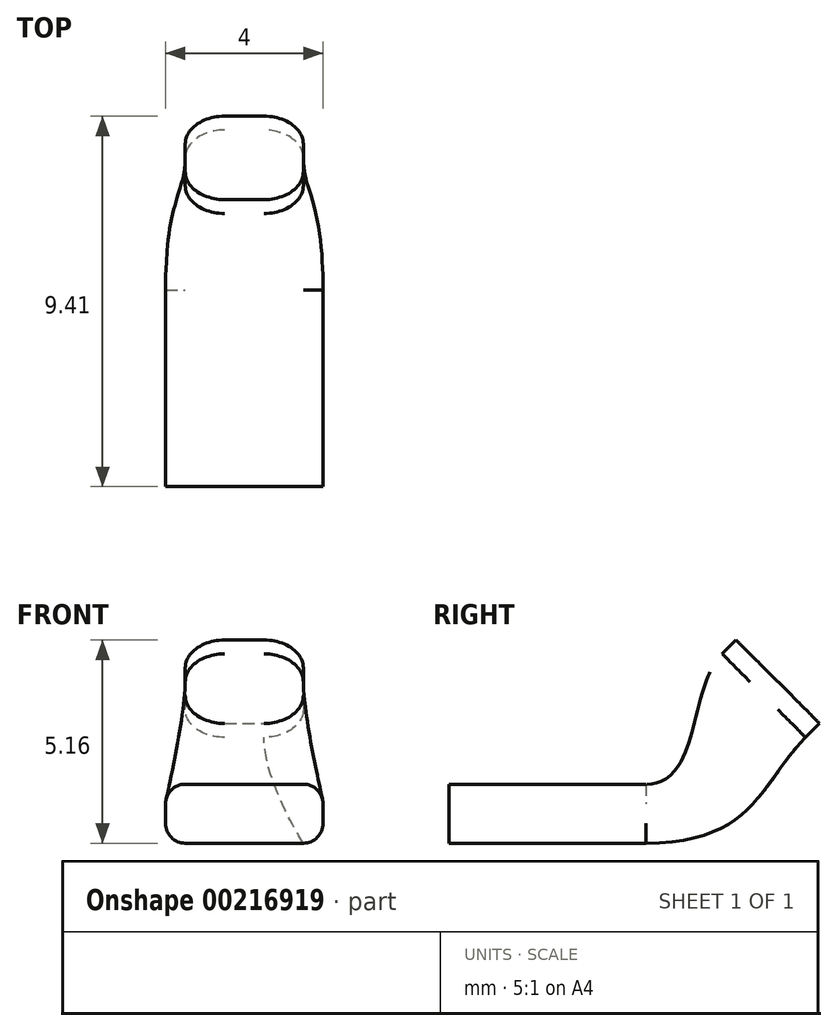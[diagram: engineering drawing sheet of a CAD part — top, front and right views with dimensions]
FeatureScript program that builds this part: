
annotation { "Feature Type Name" : "Feature", "Feature Type Description" : "" }
export const myFeature = defineFeature(function(context is Context, id is Id, definition is map)
    precondition{}
    {
        {
            var Q0;
            Q0=qCreatedBy(makeId("Right.planeOp"),FACE);
            var sketch = newSketch(context, id + "F0", { "sketchPlane" : qUnion([Q0])});
            skLineSegment(sketch, "E0", {"start": v(0, 0) * mm, "end": v(0, 5) * mm});
            skLineSegment(sketch, "E1", {"start": v(0, 5) * mm, "end": v(1, 5) * mm});
            skLineSegment(sketch, "E2", {"start": v(1, 5) * mm, "end": v(4.72, 1.28) * mm});
            skLineSegment(sketch, "E3", {"start": v(4.19, 0) * mm, "end": v(0, 0) * mm});
            skPoint(sketch, "E4.visualSharp", {"position": v(6, 0) * mm});
            skArc(sketch, "E4.filletArc", {"start": v(4.19, 0) * mm, "mid": v(4.88, 0.46) * mm, "end": v(4.72, 1.28) * mm});
            skSolve(sketch);
        }
        {
            var Q0;
            Q0=qCreatedBy(makeId("Front.planeOp"),FACE);
            var sketch = newSketch(context, id + "F1", { "sketchPlane" : qUnion([Q0])});
            skLineSegment(sketch, "E5.bottom", {"start": v(1.5, -0.75) * mm, "end": v(-1.5, -0.75) * mm});
            skLineSegment(sketch, "E5.top", {"start": v(1.5, 0.75) * mm, "end": v(-1.5, 0.75) * mm});
            skLineSegment(sketch, "E5.left", {"start": v(2, -0.25) * mm, "end": v(2, 0.25) * mm});
            skLineSegment(sketch, "E5.right", {"start": v(-2, -0.25) * mm, "end": v(-2, 0.25) * mm});
            skPoint(sketch, "E5.middle", {"position": v(0, 0) * mm});
            skPoint(sketch, "E6.visualSharp", {"position": v(2, 0.75) * mm});
            skArc(sketch, "E6.filletArc", {"start": v(2, 0.25) * mm, "mid": v(1.85, 0.6) * mm, "end": v(1.5, 0.75) * mm});
            skPoint(sketch, "E7.visualSharp", {"position": v(2, -0.75) * mm});
            skArc(sketch, "E7.filletArc", {"start": v(1.5, -0.75) * mm, "mid": v(1.85, -0.6) * mm, "end": v(2, -0.25) * mm});
            skPoint(sketch, "E8.visualSharp", {"position": v(-2, 0.75) * mm});
            skArc(sketch, "E8.filletArc", {"start": v(-1.5, 0.75) * mm, "mid": v(-1.85, 0.6) * mm, "end": v(-2, 0.25) * mm});
            skPoint(sketch, "E9.visualSharp", {"position": v(-2, -0.75) * mm});
            skArc(sketch, "E9.filletArc", {"start": v(-2, -0.25) * mm, "mid": v(-1.85, -0.6) * mm, "end": v(-1.5, -0.75) * mm});
            skSolve(sketch);
        }
        {
            var Q0;
            Q0=sQuery(id+"F0.wireOp",EDGE,"E2");
            cPlane(context, id + "F2", {"entities" : qUnion([Q0]), "cplaneType" : CPlaneType.LINE_ANGLE, "offset" : 25 * mm, "angle" : 0 * degree, "width" : 150 * mm, "height" : 150 * mm});
        }
        {
            var Q0;
            Q0=qCreatedBy(id+"F2.planeOp",FACE);
            var sketch = newSketch(context, id + "F3", { "sketchPlane" : qUnion([Q0])});
            skLineSegment(sketch, "E10.bottom", {"start": v(0.5, 1.5) * mm, "end": v(-0.5, 1.5) * mm});
            skLineSegment(sketch, "E10.top", {"start": v(0.5, -1.5) * mm, "end": v(-0.5, -1.5) * mm});
            skLineSegment(sketch, "E10.left", {"start": v(1.5, 0.5) * mm, "end": v(1.5, -0.5) * mm});
            skLineSegment(sketch, "E10.right", {"start": v(-1.5, 0.5) * mm, "end": v(-1.5, -0.5) * mm});
            skPoint(sketch, "E10.middle", {"position": v(0, 0) * mm});
            skPoint(sketch, "E11.visualSharp", {"position": v(-1.5, -1.5) * mm});
            skArc(sketch, "E11.filletArc", {"start": v(-1.5, -0.5) * mm, "mid": v(-1.2, -1.2) * mm, "end": v(-0.5, -1.5) * mm});
            skPoint(sketch, "E12.visualSharp", {"position": v(1.5, 1.5) * mm});
            skArc(sketch, "E12.filletArc", {"start": v(1.5, 0.5) * mm, "mid": v(1.2, 1.2) * mm, "end": v(0.5, 1.5) * mm});
            skPoint(sketch, "E13.visualSharp", {"position": v(-1.5, 1.5) * mm});
            skArc(sketch, "E13.filletArc", {"start": v(-0.5, 1.5) * mm, "mid": v(-1.2, 1.2) * mm, "end": v(-1.5, 0.5) * mm});
            skPoint(sketch, "E14.visualSharp", {"position": v(1.5, -1.5) * mm});
            skArc(sketch, "E14.filletArc", {"start": v(0.5, -1.5) * mm, "mid": v(1.2, -1.2) * mm, "end": v(1.5, -0.5) * mm});
            skSolve(sketch);
        }
        {
            var Q0;
            Q0=makeQuery(id+"F1.imprint","IMPRINT",FACE,{"disambiguationData":[TD([[makeQuery(id+"F1.imprint","IMPRINT",EDGE,{"derivedFrom":sQuery(id+"F1.wireOp",EDGE,"E5.bottom")}),-1.0]])]});
            extrude(context, id + "F4", {"entities" : qUnion([Q0]), "depth" : 5 * mm});
        }
        {
            var Q0;
            Q0=makeQuery(id+"F3.imprint","IMPRINT",FACE,{"disambiguationData":[TD([[makeQuery(id+"F3.imprint","IMPRINT",EDGE,{"derivedFrom":sQuery(id+"F3.wireOp",EDGE,"E11.filletArc")}),1.0]])]});
            extrude(context, id + "F5", {"entities" : qUnion([Q0]), "depth" : .5 * mm});
        }
        {
            var Q1;
            Q1=makeQuery(id+"F1.imprint","IMPRINT",FACE,{"disambiguationData":[TD([[makeQuery(id+"F1.imprint","IMPRINT",EDGE,{"derivedFrom":sQuery(id+"F1.wireOp",EDGE,"E5.bottom")}),-1.0]])]});
            var Q2;
            Q2=makeQuery(id+"F5.opExtrude","CAP_FACE",FACE,{"disambiguationData":[OSD([sQuery(id+"F3.wireOp",EDGE,"E11.filletArc"),sQuery(id+"F3.wireOp",EDGE,"E12.filletArc"),sQuery(id+"F3.wireOp",EDGE,"E13.filletArc"),sQuery(id+"F3.wireOp",EDGE,"E14.filletArc")])],"isStart":true});
            loft(context, id + "F6", {"operationType" : NewBodyOperationType.ADD, "startCondition" : LoftEndDerivativeType.NORMAL_TO_PROFILE, "startMagnitude" : 2, "endCondition" : LoftEndDerivativeType.NORMAL_TO_PROFILE, "endMagnitude" : 1, "sheetProfilesArray" : [{ "sheetProfileEntities" : qUnion([Q1]) }, { "sheetProfileEntities" : qUnion([Q2]) }]});
        }
    });
